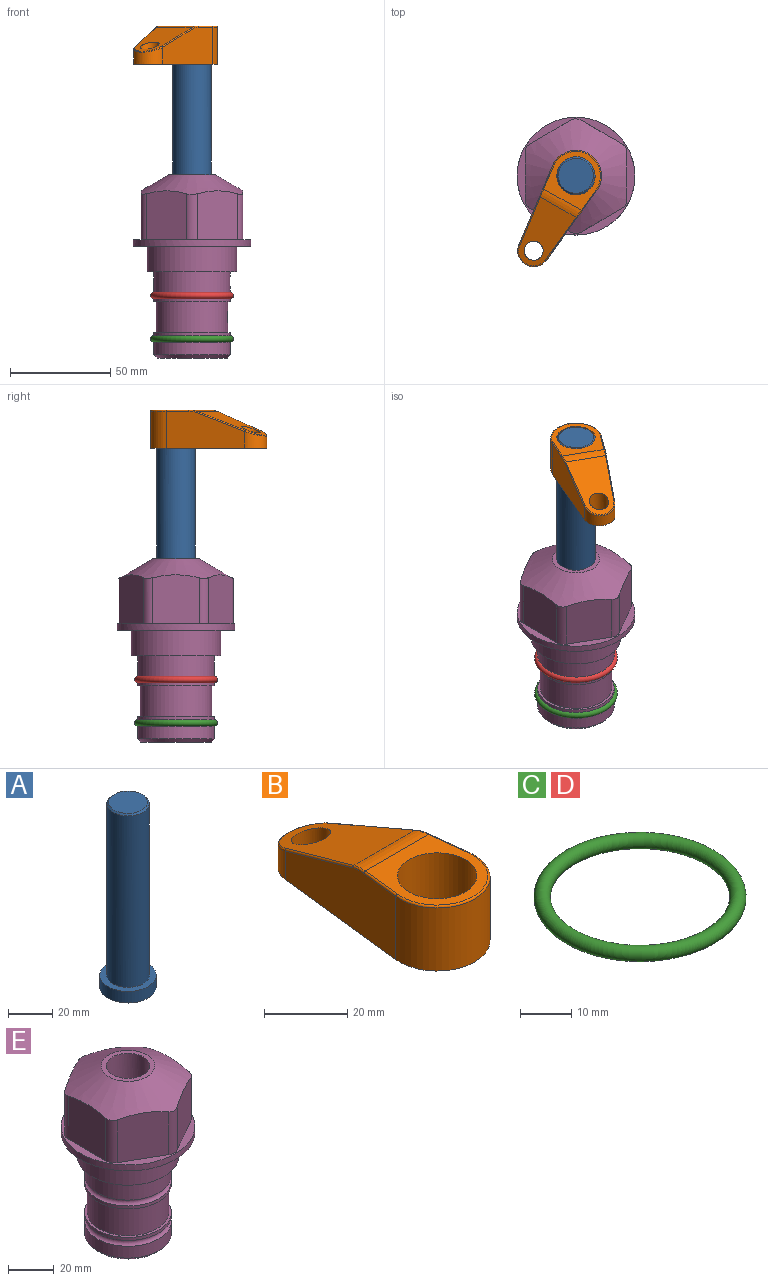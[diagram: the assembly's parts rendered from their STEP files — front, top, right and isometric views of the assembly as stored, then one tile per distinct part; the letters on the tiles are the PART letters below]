
ASSEMBLY  parts=5 mates=3
PART A: 6 faces, bbox 25.4x25.4x101.6 mm
  f0: plane 17.46x17.46mm, normal (0,0,1), area 239.5mm2, adj f5
  f1: plane 25.4x25.4mm, normal (0,0,-1), area 506.7mm2, adj f2
  f2: cylinder r=12.7mm len=25.4mm, axis (0,0,1), area 506.7mm2, adj f1,f3
  f3: plane 25.4x25.4mm, normal (0,0,1), area 221.7mm2, adj f2,f4
  f4: cylinder r=9.53mm len=94.46mm, axis (0,0,1), area 5653mm2, adj f3,f5
  f5: cone r=8.73mm half-angle=45deg, axis (0,0,-1), area 64.4mm2, adj f0,f4
PART B: 44 faces, bbox 27.5x64.5x19.1 mm
  f0: plane 2.3x0.95mm, normal (0,0,-1), area 1mm2, adj f25,f30,f34
  f1: plane 63.5x25.4mm, normal (0,0,-1), area 561.7mm2, adj f2,f3,f4,f5,f6,f7,f19,f20
  f2: cylinder r=12.7mm len=25.4mm, axis (0,0,-1), area 792.2mm2, adj f1,f3,f5,f13
  f3: plane 42.33x18.54mm, normal (0.99,0.11,0), area 647mm2, adj f1,f2,f4,f11,f12,f14
  f4: cylinder r=7.94mm len=15.78mm, axis (0,0,-1), area 158.6mm2, adj f1,f3,f5,f16
  f5: plane 42.33x18.54mm, normal (-0.99,0.11,0), area 647mm2, adj f1,f2,f4,f15,f17,f18
  f6: cylinder r=9.53mm len=19.05mm, axis (0,0,-1), area 1140.1mm2, adj f1,f8
  f7: cylinder r=4.76mm len=10.98mm, axis (0,0,-1), area 276.1mm2, adj f1,f9
  f8: plane 25.83x24.38mm, normal (0,0,1), area 262.2mm2, adj f6,f10,f11,f13,f15
  f9: plane 32.49x20.55mm, normal (0,0.34,0.94), area 489.9mm2, adj f7,f10,f14,f16,f18
  f10: cylinder r=12.7mm len=21.49mm, axis (-1,0,0), area 93.2mm2, adj f8,f9,f12,f17
  f11: cylinder r=0.51mm len=12.34mm, axis (0.11,-0.99,0), area 9.9mm2, adj f3,f8,f12,f13
  f12: bspline ~7.62x1.64mm, area 3.5mm2, adj f3,f10,f11,f14
  f13: torus R=12.19mm, axis (0,0,1), area 33.6mm2, adj f2,f8,f11,f15
  f14: cylinder r=0.51mm len=26.01mm, axis (0.1,-0.93,0.34), area 21.6mm2, adj f3,f9,f12,f16
  f15: cylinder r=0.51mm len=12.34mm, axis (0.11,0.99,0), area 9.9mm2, adj f5,f8,f13,f17
  f16: bspline ~15.78x7.05mm, area 15.7mm2, adj f4,f9,f14,f18
  f17: bspline ~7.62x1.64mm, area 3.5mm2, adj f5,f10,f15,f18
  f18: cylinder r=0.51mm len=26.01mm, axis (0.1,0.93,-0.34), area 21.6mm2, adj f5,f9,f16,f17
  f19: plane 21.6x14.29mm, normal (-0.99,-0.11,0), area 242.6mm2, adj f1,f26,f28,f34,f36,f38
  f20: plane 21.6x14.29mm, normal (0.99,-0.11,0), area 242.6mm2, adj f1,f27,f29,f37,f39,f41
  f21: cylinder r=12.7mm len=14.29mm, axis (0,0,-1), area 173.2mm2, adj f1,f26,f27,f30,f31,f33
  f22: cylinder r=7.94mm len=7.63mm, axis (0,0,-1), area 53.8mm2, adj f1,f28,f29,f42
  f23: plane 2.3x0.95mm, normal (0,0,-1), area 1mm2, adj f25,f33,f37
  f24: plane 17.94x12.32mm, normal (0,-0.34,-0.94), area 191.2mm2, adj f25,f38,f41,f42
  f25: cylinder r=9.53mm len=12.93mm, axis (-1,0,0), area 37.5mm2, adj f0,f23,f24,f31,f36,f39
  f26: cylinder r=1.59mm len=14.29mm, axis (0,0,-1), area 49mm2, adj f1,f19,f21,f32
  f27: cylinder r=1.59mm len=14.29mm, axis (0,0,-1), area 49mm2, adj f1,f20,f21,f35
  f28: cylinder r=1.59mm len=7.28mm, axis (0,0,-1), area 22.1mm2, adj f1,f19,f22,f40
  f29: cylinder r=1.59mm len=7.28mm, axis (0,0,-1), area 22.1mm2, adj f1,f20,f22,f43
  f30: torus R=14.29mm, axis (0,0,1), area 5.8mm2, adj f0,f21,f31,f32
  f31: bspline ~11.06x2.73mm, area 20.8mm2, adj f21,f25,f30,f33
  f32: sphere r=1.59mm, area 5.4mm2, adj f26,f30,f34
  f33: torus R=14.29mm, axis (0,0,1), area 5.8mm2, adj f21,f23,f31,f35
  f34: cylinder r=1.59mm len=1.68mm, axis (-0.11,0.99,0), area 2.4mm2, adj f0,f19,f32,f36
  f35: sphere r=1.59mm, area 5.4mm2, adj f27,f33,f37
  f36: bspline ~5.82x2.33mm, area 7.7mm2, adj f19,f25,f34,f38
  f37: cylinder r=1.59mm len=1.68mm, axis (0.11,0.99,0), area 2.4mm2, adj f20,f23,f35,f39
  f38: cylinder r=1.59mm len=18.33mm, axis (0.1,-0.93,0.34), area 46.7mm2, adj f19,f24,f36,f40
  f39: bspline ~5.82x2.33mm, area 7.7mm2, adj f20,f25,f37,f41
  f40: sphere r=1.59mm, area 3.6mm2, adj f28,f38,f42
  f41: cylinder r=1.59mm len=18.33mm, axis (0.1,0.93,-0.34), area 46.7mm2, adj f20,f24,f39,f43
  f42: bspline ~8.31x1.84mm, area 15.3mm2, adj f22,f24,f40,f43
  f43: sphere r=1.59mm, area 3.6mm2, adj f29,f41,f42
PART C: 1 faces, bbox 44.7x44.7x3.2 mm
  f0: torus R=19.05mm, axis (0,0,1), area 1193.9mm2
PART D: same geometry as C
PART E: 36 faces, bbox 58.7x58.7x91.2 mm
  f0: cylinder r=17.78mm len=35.56mm, axis (0,0,1), area 1670.8mm2, adj f23,f24,f31
  f1: cylinder r=19.05mm len=38.1mm, axis (0,0,1), area 1191.9mm2, adj f26,f27,f30
  f2: plane 58.66x58.66mm, normal (0,0,-1), area 1150.6mm2, adj f3,f28
  f3: cylinder r=29.33mm len=58.66mm, axis (0,0,-1), area 585.1mm2, adj f2,f4
  f4: plane 58.66x58.66mm, normal (0,0,1), area 475.9mm2, adj f3,f5,f6,f7,f8,f9,f10,f11
  f5: plane 24.5x20.32mm, normal (-0.5,0.87,0), area 562.8mm2, adj f4,f15,f16,f17
  f6: plane 24.5x20.32mm, normal (0.5,0.87,0), area 562.8mm2, adj f4,f14,f15,f17
  f7: plane 24.5x23.48mm, normal (1,0,0), area 562.8mm2, adj f4,f13,f14,f17
  f8: plane 24.5x20.32mm, normal (0.5,-0.87,0), area 562.8mm2, adj f4,f12,f13,f17
  f9: plane 24.5x20.32mm, normal (-0.5,-0.87,0), area 562.8mm2, adj f4,f11,f12,f17
  f10: plane 24.5x23.48mm, normal (-1,0,0), area 562.8mm2, adj f4,f11,f16,f17
  f11: cylinder r=5.08mm len=23.01mm, axis (0,0,-1), area 121.2mm2, adj f4,f9,f10,f17
  f12: cylinder r=5.08mm len=23.01mm, axis (0,0,-1), area 121.2mm2, adj f4,f8,f9,f17
  f13: cylinder r=5.08mm len=23.01mm, axis (0,0,-1), area 121.2mm2, adj f4,f7,f8,f17
  f14: cylinder r=5.08mm len=23.01mm, axis (0,0,-1), area 121.2mm2, adj f4,f6,f7,f17
  f15: cylinder r=5.08mm len=23.01mm, axis (0,0,-1), area 121.2mm2, adj f4,f5,f6,f17
  f16: cylinder r=5.08mm len=23.01mm, axis (0,0,-1), area 121.2mm2, adj f4,f5,f10,f17
  f17: cone r=11.73mm half-angle=60deg, axis (0,0,-1), area 2071.8mm2, adj f5,f6,f7,f8,f9,f10,f11,f12
  f18: plane 23.46x23.46mm, normal (0,0,1), area 147.4mm2, adj f17,f35
  f19: plane 34.93x34.93mm, normal (0,0,-1), area 958mm2, adj f29
  f20: cylinder r=19.05mm len=38.1mm, axis (0,0,1), area 760.1mm2, adj f21,f29
  f21: torus R=19.05mm, axis (0,0,1), area 565.3mm2, adj f20,f22
  f22: cylinder r=19.05mm len=38.1mm, axis (0,0,1), area 190mm2, adj f21,f23
  f23: plane 38.1x38.1mm, normal (0,0,1), area 146.9mm2, adj f0,f22
  f24: plane 38.1x38.1mm, normal (0,0,-1), area 146.9mm2, adj f0,f25
  f25: cylinder r=19.05mm len=38.1mm, axis (0,0,1), area 190mm2, adj f24,f26
  f26: torus R=19.05mm, axis (0,0,1), area 565.3mm2, adj f1,f25
  f27: plane 44.45x44.45mm, normal (0,0,-1), area 411.7mm2, adj f1,f28
  f28: cylinder r=22.23mm len=44.45mm, axis (0,0,1), area 1773.5mm2, adj f2,f27
  f29: cone r=19.05mm half-angle=45deg, axis (0,0,1), area 257.5mm2, adj f19,f20
  f30: cylinder r=3.17mm len=6.75mm, axis (-1,0,0), area 128mm2, adj f1,f33
  f31: cylinder r=3.17mm len=6.35mm, axis (-1,0,0), area 102.5mm2, adj f0,f33
  f32: plane 25.4x25.4mm, normal (0,0,1), area 506.7mm2, adj f33
  f33: cylinder r=12.7mm len=66.42mm, axis (0,0,-1), area 5236.2mm2, adj f30,f31,f32,f34
  f34: cone r=9.53mm half-angle=30deg, axis (0,0,-1), area 443.4mm2, adj f33,f35
  f35: cylinder r=9.53mm len=19.05mm, axis (0,0,-1), area 849mm2, adj f18,f34
PLACE A rot(axis=(0,0,-1),119.5deg) t=(0,0,36.13)mm
PLACE B rot(axis=(0,0,1),150.5deg) t=(0,0,90.74)mm
PLACE C t=(0,0,-21.59)mm
PLACE D at identity
PLACE E at identity fixed
MATE fastened C.f0 <-> E.f0  axis (0,0,1) through (0,0,-46.1)mm
MATE cylindrical A.f2 <-> E.f0  axis (0,0,1) through (0,0,61.77)mm
MATE fastened B.f2 <-> A.f2  axis (0,0,1) through (0,0,109.79)mm
